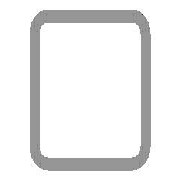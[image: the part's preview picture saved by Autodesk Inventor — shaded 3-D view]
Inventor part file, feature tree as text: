
AUTODESK INVENTOR PART (.ipt)
format: ipt  version: 2025 (Build 290162010, 162A)  size: 134,144 bytes
history: native  units: mm (DEFAULTED — no unit token found)
features: other x4, sketch x1, plane x1
ambient origin geometry x8: Origin, YZ Plane, XZ Plane, XY Plane, X Axis, Y Axis, Z Axis, Center Point
bodies: Solid1 (feature_tree), Body (feature_tree)
feature tree (6):
  parser-record x1  (decoder bookkeeping rows leaked as tree rows — omitted from the tree; the rows remain in map.json)
  other  "Driven Length"
  other  "Start Plane"
  other  "End Plane"
  sketch  "Sketch3"  dims[d3=858.0mm d4=0.0mm d7=4.0mm d9=40.0mm d11=40.0mm d12=2.0mm d13=40.0mm d14=898.0mm d15=20.0mm d16=20.0mm d17=90.0deg d18=858.0mm]
  plane  "Work Plane3"
